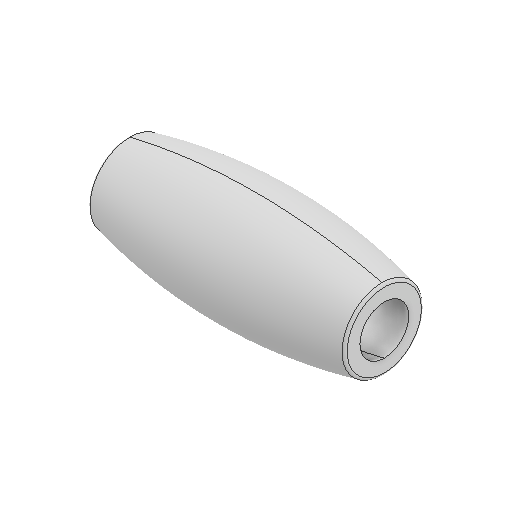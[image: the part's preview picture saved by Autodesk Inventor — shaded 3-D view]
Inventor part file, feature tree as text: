
AUTODESK INVENTOR PART (.ipt)
format: ipt  version: 2024.1 (Build 281209000, 209)  size: 179,200 bytes
history: native  units: in
note: dims shown in document units (in); Inventor stores cm internally (conversion verified against a paired STEP export)
features: fillet x1
ambient origin geometry x8: Origin, YZ Plane, XZ Plane, XY Plane, X Axis, Y Axis, Z Axis, Center Point
bodies: Solid1 (feature_tree)
feature tree (1):
  fillet  "Fillet1"  [1 undecoded]
note: 1 required parameter value undecoded (feature->parameter linkage not recoverable at this tier; creation-order binding heuristic only, values carry confidence <= 0.55)
